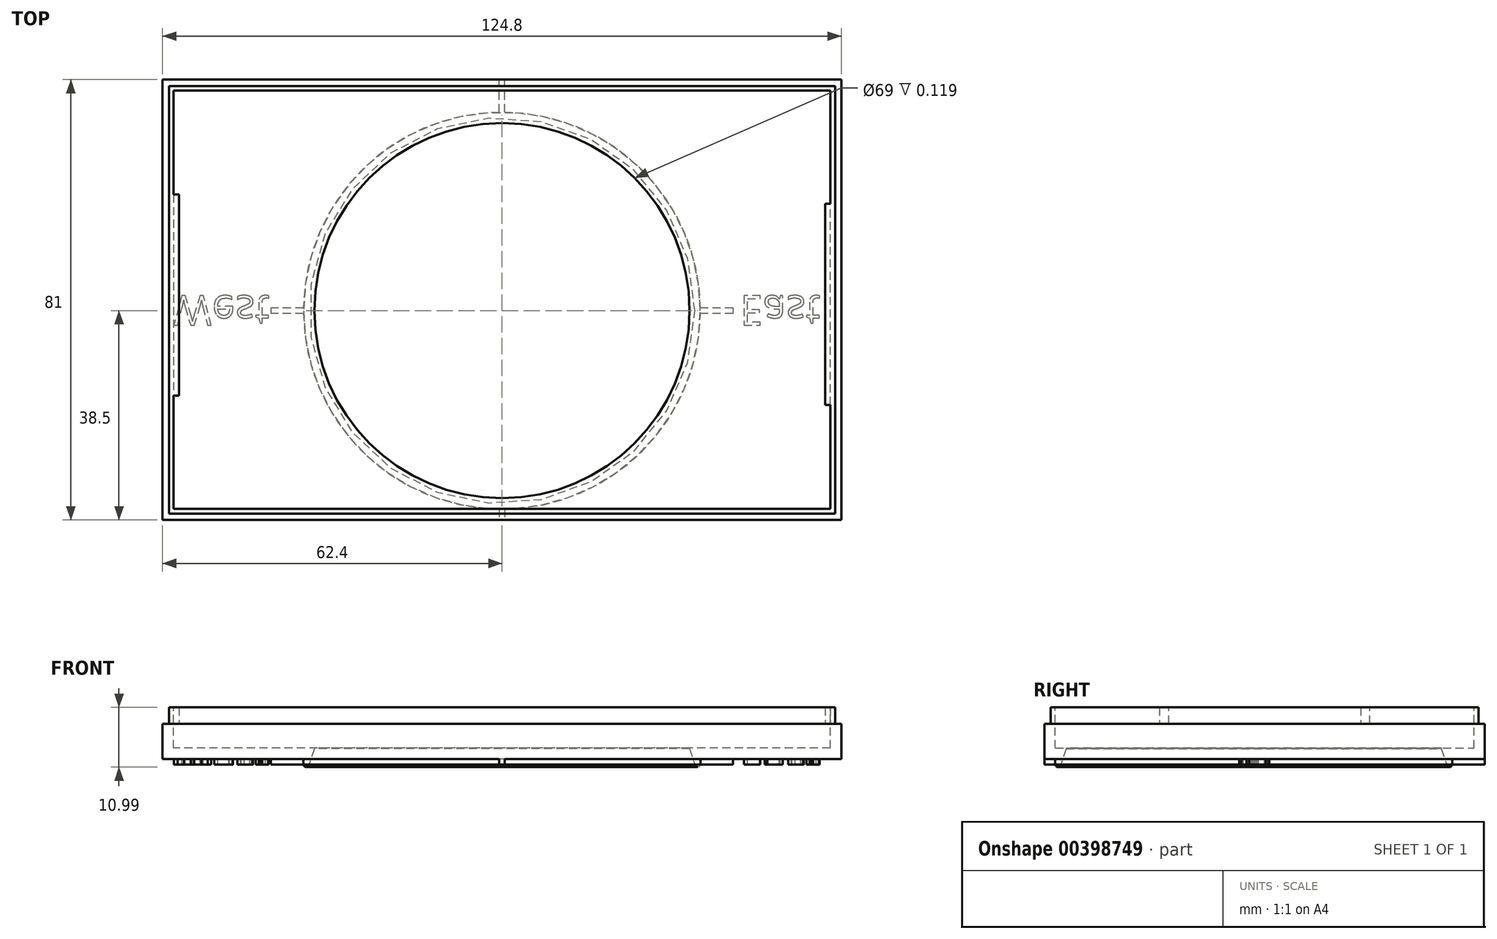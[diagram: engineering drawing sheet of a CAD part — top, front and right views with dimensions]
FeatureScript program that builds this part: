
annotation { "Feature Type Name" : "Feature", "Feature Type Description" : "" }
export const myFeature = defineFeature(function(context is Context, id is Id, definition is map)
    precondition{}
    {
        {
            var Q0;
            Q0=qCreatedBy(makeId("Top.planeOp"),FACE);
            var sketch = newSketch(context, id + "F0", { "sketchPlane" : qUnion([Q0])});
            skLineSegment(sketch, "E0.bottom", {"start": v(62.4, -40.5) * mm, "end": v(-62.4, -40.5) * mm});
            skLineSegment(sketch, "E0.top", {"start": v(62.4, 40.5) * mm, "end": v(-62.4, 40.5) * mm});
            skLineSegment(sketch, "E0.left", {"start": v(62.4, -40.5) * mm, "end": v(62.4, 40.5) * mm});
            skLineSegment(sketch, "E0.right", {"start": v(-62.4, -40.5) * mm, "end": v(-62.4, 40.5) * mm});
            skPoint(sketch, "E0.middle", {"position": v(0, 0) * mm});
            skSolve(sketch);
        }
        {
            var Q0;
            Q0 = qSketchRegion(id + "F0", true);
            extrude(context, id + "F1", {"entities" : qUnion([Q0]), "depth" : 9.5 * mm, "offsetDistance" : 25 * mm});
        }
        {
            var Q0;
            Q0=makeQuery(id+"F1.opExtrude","CAP_FACE",FACE,{"disambiguationData":[OSD([sQuery(id+"F0.wireOp",EDGE,"E0.bottom"),sQuery(id+"F0.wireOp",EDGE,"E0.top"),sQuery(id+"F0.wireOp",EDGE,"E0.left"),sQuery(id+"F0.wireOp",EDGE,"E0.right")])],"isStart":false});
            var sketch = newSketch(context, id + "F2", { "sketchPlane" : qUnion([Q0])});
            skLineSegment(sketch, "E1.bottom", {"start": v(60.4, -38.5) * mm, "end": v(-60.4, -38.5) * mm});
            skLineSegment(sketch, "E1.top", {"start": v(60.4, 38.5) * mm, "end": v(-60.4, 38.5) * mm});
            skLineSegment(sketch, "E1.left", {"start": v(60.4, -38.5) * mm, "end": v(60.4, 38.5) * mm});
            skLineSegment(sketch, "E1.right", {"start": v(-60.4, -38.5) * mm, "end": v(-60.4, 38.5) * mm});
            skPoint(sketch, "E1.middle", {"position": v(0, 0) * mm});
            skSolve(sketch);
        }
        {
            var Q0;
            Q0=makeQuery(id+"F2.imprint","IMPRINT",FACE,{"disambiguationData":[TD([[makeQuery(id+"F2.imprint","IMPRINT",EDGE,{"derivedFrom":sQuery(id+"F2.wireOp",EDGE,"E1.bottom")}),-1.0]])]});
            extrude(context, id + "F3", {"entities" : qUnion([Q0]), "operationType" : NewBodyOperationType.REMOVE, "oppositeDirection" : true, "depth" : 7.5 * mm, "offsetDistance" : 25 * mm});
        }
        {
            var Q0;
            Q0=makeQuery(id+"F1.opExtrude","CAP_FACE",FACE,{"disambiguationData":[OSD([sQuery(id+"F0.wireOp",EDGE,"E0.bottom"),sQuery(id+"F0.wireOp",EDGE,"E0.top"),sQuery(id+"F0.wireOp",EDGE,"E0.left"),sQuery(id+"F0.wireOp",EDGE,"E0.right")])],"isStart":true});
            var sketch = newSketch(context, id + "F4", { "sketchPlane" : qUnion([Q0])});
            skCircle(sketch, "E2", {"center": v(0, 2) * mm, "radius": 36.5 * mm});
            skSolve(sketch);
        }
        {
            var Q0;
            Q0=makeQuery(id+"F4.imprint","IMPRINT",FACE,{"disambiguationData":[TD([[makeQuery(id+"F4.imprint","IMPRINT",EDGE,{"derivedFrom":sQuery(id+"F4.wireOp",EDGE,"E2")}),1.0]])]});
            extrude(context, id + "F5", {"entities" : qUnion([Q0]), "operationType" : NewBodyOperationType.ADD, "depth" : 1 * mm});
        }
        {
            var Q0;
            Q0=makeQuery(id+"F5.opExtrude","CAP_FACE",FACE,{"disambiguationData":[OSD([sQuery(id+"F4.wireOp",EDGE,"E2")])],"isStart":false});
            var sketch = newSketch(context, id + "F6", { "sketchPlane" : qUnion([Q0])});
            skCircle(sketch, "E3", {"center": v(0, 2) * mm, "radius": 34.5 * mm});
            skSolve(sketch);
        }
        {
            var Q0;
            Q0=makeQuery(id+"F6.imprint","IMPRINT",FACE,{"disambiguationData":[TD([[makeQuery(id+"F6.imprint","IMPRINT",EDGE,{"derivedFrom":sQuery(id+"F6.wireOp",EDGE,"E3")}),1.0]])]});
            extrude(context, id + "F7", {"entities" : qUnion([Q0]), "operationType" : NewBodyOperationType.REMOVE, "endBound" : BoundingType.THROUGH_ALL, "oppositeDirection" : true, "depth" : 25 * mm});
        }
        {
            var Q0;
            Q0=qCreatedBy(makeId("Top.planeOp"),FACE);
            var sketch = newSketch(context, id + "F8", { "sketchPlane" : qUnion([Q0])});
            skCircle(sketch, "E4", {"center": v(0, -2) * mm, "radius": 35.5 * mm});
            skSolve(sketch);
        }
        {
            var Q0;
            Q0=qCreatedBy(makeId("Front.planeOp"),FACE);
            var sketch = newSketch(context, id + "F9", { "sketchPlane" : qUnion([Q0])});
            skLineSegment(sketch, "E5", {"start": v(34.42, -1.03) * mm, "end": v(35.42, -1.03) * mm});
            skLineSegment(sketch, "E6", {"start": v(35.42, -1.03) * mm, "end": v(34.39, 2.05) * mm});
            skLineSegment(sketch, "E7", {"start": v(34.39, 2.05) * mm, "end": v(34.42, -1.03) * mm});
            skSolve(sketch);
        }
        {
            var Q0;
            Q0 = qSketchRegion(id + "F9", true);
            var Q1;
            Q1 = qConstructionFilter(qBodyType(qCreatedBy(id + "F8" ,EDGE), BodyType.WIRE), ConstructionObject.NO);
            sweep(context, id + "F10", {"operationType" : NewBodyOperationType.REMOVE, "profiles" : qUnion([Q0]), "path" : qUnion([Q1])});
        }
        {
            var Q0;
            Q0=qCreatedBy(makeId("Top.planeOp"),FACE);
            cPlane(context, id + "F11", {"entities" : qUnion([Q0]), "cplaneType" : CPlaneType.OFFSET, "offset" : 1 * mm, "oppositeDirection" : true, "width" : 150 * mm, "height" : 150 * mm});
        }
        {
            var Q0;
            Q0=qCreatedBy(id+"F11.planeOp",FACE);
            var sketch = newSketch(context, id + "F12", { "sketchPlane" : qUnion([Q0])});
            skCircle(sketch, "E8", {"center": v(0, -2) * mm, "radius": 36 * mm});
            skSolve(sketch);
        }
        {
            var Q0;
            Q0=qCreatedBy(makeId("Front.planeOp"),FACE);
            var sketch = newSketch(context, id + "F13", { "sketchPlane" : qUnion([Q0])});
            skCircle(sketch, "E9", {"center": v(35.91, -1) * mm, "radius": 0.5 * mm});
            skSolve(sketch);
        }
        {
            var Q0;
            Q0=makeQuery(id+"F13.imprint","IMPRINT",FACE,{"disambiguationData":[TD([[makeQuery(id+"F13.imprint","IMPRINT",EDGE,{"derivedFrom":sQuery(id+"F13.wireOp",EDGE,"E9")}),1.0]])]});
            var Q1;
            Q1=sQuery(id+"F12.wireOp",EDGE,"E8");
            revolve(context, id + "F14", {"operationType" : NewBodyOperationType.ADD, "entities" : qUnion([Q0]), "axis" : qUnion([Q1]), "revolveType" : RevolveType.FULL});
        }
        {
            var Q0;
            Q0=makeQuery(id+"F1.opExtrude","CAP_FACE",FACE,{"disambiguationData":[OSD([sQuery(id+"F0.wireOp",EDGE,"E0.bottom"),sQuery(id+"F0.wireOp",EDGE,"E0.top"),sQuery(id+"F0.wireOp",EDGE,"E0.left"),sQuery(id+"F0.wireOp",EDGE,"E0.right")])],"isStart":true});
            var sketch = newSketch(context, id + "F15", { "sketchPlane" : qUnion([Q0])});
            skLineSegment(sketch, "E10.bottom", {"start": v(-36.5, 1.5) * mm, "end": v(-42.5, 1.5) * mm});
            skLineSegment(sketch, "E10.top", {"start": v(-36.5, 2.5) * mm, "end": v(-42.5, 2.5) * mm});
            skLineSegment(sketch, "E10.left", {"start": v(-36.5, 1.5) * mm, "end": v(-36.5, 2.5) * mm});
            skLineSegment(sketch, "E10.right", {"start": v(-42.5, 1.5) * mm, "end": v(-42.5, 2.5) * mm});
            skPoint(sketch, "E10.middle", {"position": v(-39.5, 2) * mm});
            skSolve(sketch);
        }
        {
            var Q0;
            Q0 = qSketchRegion(id + "F15", true);
            extrude(context, id + "F16", {"entities" : qUnion([Q0]), "operationType" : NewBodyOperationType.ADD, "depth" : 1 * mm});
        }
        {
            var Q0;
            Q0=makeQuery(id+"F1.opExtrude","CAP_FACE",FACE,{"disambiguationData":[OSD([sQuery(id+"F0.wireOp",EDGE,"E0.bottom"),sQuery(id+"F0.wireOp",EDGE,"E0.top"),sQuery(id+"F0.wireOp",EDGE,"E0.left"),sQuery(id+"F0.wireOp",EDGE,"E0.right")])],"isStart":true});
            var sketch = newSketch(context, id + "F17", { "sketchPlane" : qUnion([Q0])});
            skLineSegment(sketch, "E11.bottom", {"start": v(42.5, 1.5) * mm, "end": v(36.5, 1.5) * mm});
            skLineSegment(sketch, "E11.top", {"start": v(42.5, 2.5) * mm, "end": v(36.5, 2.5) * mm});
            skLineSegment(sketch, "E11.left", {"start": v(42.5, 1.5) * mm, "end": v(42.5, 2.5) * mm});
            skLineSegment(sketch, "E11.right", {"start": v(36.5, 1.5) * mm, "end": v(36.5, 2.5) * mm});
            skPoint(sketch, "E11.middle", {"position": v(39.5, 2) * mm});
            skSolve(sketch);
        }
        {
            var Q0;
            Q0 = qSketchRegion(id + "F17", true);
            extrude(context, id + "F18", {"entities" : qUnion([Q0]), "operationType" : NewBodyOperationType.ADD, "depth" : 1 * mm});
        }
        {
            var Q0;
            Q0=makeQuery(id+"F1.opExtrude","CAP_FACE",FACE,{"disambiguationData":[OSD([sQuery(id+"F0.wireOp",EDGE,"E0.bottom"),sQuery(id+"F0.wireOp",EDGE,"E0.top"),sQuery(id+"F0.wireOp",EDGE,"E0.left"),sQuery(id+"F0.wireOp",EDGE,"E0.right")])],"isStart":true});
            var sketch = newSketch(context, id + "F19", { "sketchPlane" : qUnion([Q0])});
            skLineSegment(sketch, "E12.bottom", {"start": v(0.5, -34.47) * mm, "end": v(-0.5, -34.47) * mm});
            skLineSegment(sketch, "E12.top", {"start": v(0.5, -40.47) * mm, "end": v(-0.5, -40.47) * mm});
            skLineSegment(sketch, "E12.left", {"start": v(0.5, -34.47) * mm, "end": v(0.5, -40.47) * mm});
            skLineSegment(sketch, "E12.right", {"start": v(-0.5, -34.47) * mm, "end": v(-0.5, -40.47) * mm});
            skPoint(sketch, "E12.middle", {"position": v(0, -37.47) * mm});
            skSolve(sketch);
        }
        {
            var Q0;
            Q0 = qSketchRegion(id + "F19", true);
            extrude(context, id + "F20", {"entities" : qUnion([Q0]), "operationType" : NewBodyOperationType.ADD, "depth" : 1 * mm});
        }
        {
            var Q0;
            Q0=makeQuery(id+"F1.opExtrude","CAP_FACE",FACE,{"disambiguationData":[OSD([sQuery(id+"F0.wireOp",EDGE,"E0.bottom"),sQuery(id+"F0.wireOp",EDGE,"E0.top"),sQuery(id+"F0.wireOp",EDGE,"E0.left"),sQuery(id+"F0.wireOp",EDGE,"E0.right")])],"isStart":true});
            var sketch = newSketch(context, id + "F21", { "sketchPlane" : qUnion([Q0])});
            skLineSegment(sketch, "E13.bottom", {"start": v(0.5, 38.5) * mm, "end": v(-0.5, 38.5) * mm});
            skLineSegment(sketch, "E13.top", {"start": v(0.5, 40.5) * mm, "end": v(-0.5, 40.5) * mm});
            skLineSegment(sketch, "E13.left", {"start": v(0.5, 38.5) * mm, "end": v(0.5, 40.5) * mm});
            skLineSegment(sketch, "E13.right", {"start": v(-0.5, 38.5) * mm, "end": v(-0.5, 40.5) * mm});
            skPoint(sketch, "E13.middle", {"position": v(0, 39.5) * mm});
            skSolve(sketch);
        }
        {
            var Q0;
            Q0 = qSketchRegion(id + "F21", true);
            extrude(context, id + "F22", {"entities" : qUnion([Q0]), "operationType" : NewBodyOperationType.ADD, "depth" : 1 * mm});
        }
        {
            var Q0;
            Q0=makeQuery(id+"F1.opExtrude","CAP_FACE",FACE,{"disambiguationData":[OSD([sQuery(id+"F0.wireOp",EDGE,"E0.bottom"),sQuery(id+"F0.wireOp",EDGE,"E0.top"),sQuery(id+"F0.wireOp",EDGE,"E0.left"),sQuery(id+"F0.wireOp",EDGE,"E0.right")])],"isStart":true});
            var sketch = newSketch(context, id + "F23", { "sketchPlane" : qUnion([Q0])});
            skText(sketch, "E14", { "text": " West", "fontName": "OpenSans-Regular.ttf"});
            const initialGuessF23  = {"E14": [-0.0624, -0.00075, 1, 0, 0.0055]};
            skSetInitialGuess(sketch, initialGuessF23);
            skSolve(sketch);
        }
        {
            var Q0;
            Q0 = qSketchRegion(id + "F23", true);
            extrude(context, id + "F24", {"entities" : qUnion([Q0]), "operationType" : NewBodyOperationType.ADD, "depth" : 1 * mm});
        }
        {
            var Q0;
            {var subQ0=sQuery(id+"F0.wireOp",EDGE,"E0.right");var subQ1=sQuery(id+"F0.wireOp",EDGE,"E0.left");var subQ2=sQuery(id+"F0.wireOp",EDGE,"E0.bottom");var subQ3=sQuery(id+"F0.wireOp",EDGE,"E0.top");Q0=makeQuery(id+"F24.boolean.opBoolean","SPLIT",FACE,{"disambiguationData":[TD([makeQuery(id+"F1.opExtrude","SWEPT_FACE",FACE,{"disambiguationData":[OSD([subQ2])]})])],"derivedFrom":makeQuery(id+"F1.opExtrude","CAP_FACE",FACE,{"disambiguationData":[OSD([subQ2,subQ3,subQ1,subQ0])],"isStart":true})});}
            var sketch = newSketch(context, id + "F25", { "sketchPlane" : qUnion([Q0])});
            skText(sketch, "E15", { "text": "East", "fontName": "OpenSans-Regular.ttf"});
            const initialGuessF25  = {"E15": [0.04373, -0.00075, 1, 0, 0.0055]};
            skSetInitialGuess(sketch, initialGuessF25);
            skSolve(sketch);
        }
        {
            var Q0;
            Q0 = qSketchRegion(id + "F25", true);
            extrude(context, id + "F26", {"entities" : qUnion([Q0]), "operationType" : NewBodyOperationType.ADD, "depth" : 1 * mm});
        }
        {
            var Q0;
            Q0=makeQuery(id+"F1.opExtrude","CAP_FACE",FACE,{"disambiguationData":[OSD([sQuery(id+"F0.wireOp",EDGE,"E0.bottom"),sQuery(id+"F0.wireOp",EDGE,"E0.top"),sQuery(id+"F0.wireOp",EDGE,"E0.left"),sQuery(id+"F0.wireOp",EDGE,"E0.right")])],"isStart":false});
            var sketch = newSketch(context, id + "F27", { "sketchPlane" : qUnion([Q0])});
            skLineSegment(sketch, "E16.bottom", {"start": v(-62.4, -40.5) * mm, "end": v(-61.25, -40.5) * mm});
            skLineSegment(sketch, "E16.top", {"start": v(-62.4, 40.5) * mm, "end": v(-61.25, 40.5) * mm});
            skLineSegment(sketch, "E16.left", {"start": v(-62.4, -40.5) * mm, "end": v(-62.4, 40.5) * mm});
            skLineSegment(sketch, "E16.right", {"start": v(-61.25, -40.5) * mm, "end": v(-61.25, 40.5) * mm});
            skSolve(sketch);
        }
        {
            var Q0;
            Q0 = qSketchRegion(id + "F27", true);
            extrude(context, id + "F28", {"entities" : qUnion([Q0]), "operationType" : NewBodyOperationType.REMOVE, "oppositeDirection" : true, "depth" : 3 * mm, "offsetDistance" : 25 * mm});
        }
        {
            var Q0;
            Q0=makeQuery(id+"F1.opExtrude","CAP_FACE",FACE,{"disambiguationData":[OSD([sQuery(id+"F0.wireOp",EDGE,"E0.bottom"),sQuery(id+"F0.wireOp",EDGE,"E0.top"),sQuery(id+"F0.wireOp",EDGE,"E0.left"),sQuery(id+"F0.wireOp",EDGE,"E0.right")])],"isStart":false});
            var sketch = newSketch(context, id + "F29", { "sketchPlane" : qUnion([Q0])});
            skLineSegment(sketch, "E17.bottom", {"start": v(62.4, -40.5) * mm, "end": v(61.25, -40.5) * mm});
            skLineSegment(sketch, "E17.top", {"start": v(62.4, 40.5) * mm, "end": v(61.25, 40.5) * mm});
            skLineSegment(sketch, "E17.left", {"start": v(62.4, -40.5) * mm, "end": v(62.4, 40.5) * mm});
            skLineSegment(sketch, "E17.right", {"start": v(61.25, -40.5) * mm, "end": v(61.25, 40.5) * mm});
            skSolve(sketch);
        }
        {
            var Q0;
            Q0 = qSketchRegion(id + "F29", true);
            extrude(context, id + "F30", {"entities" : qUnion([Q0]), "operationType" : NewBodyOperationType.REMOVE, "oppositeDirection" : true, "depth" : 3 * mm, "offsetDistance" : 25 * mm});
        }
        {
            var Q0;
            Q0=makeQuery(id+"F1.opExtrude","CAP_FACE",FACE,{"disambiguationData":[OSD([sQuery(id+"F0.wireOp",EDGE,"E0.bottom"),sQuery(id+"F0.wireOp",EDGE,"E0.top"),sQuery(id+"F0.wireOp",EDGE,"E0.left"),sQuery(id+"F0.wireOp",EDGE,"E0.right")])],"isStart":false});
            var sketch = newSketch(context, id + "F31", { "sketchPlane" : qUnion([Q0])});
            skLineSegment(sketch, "E18.bottom", {"start": v(-61.25, 40.5) * mm, "end": v(61.25, 40.5) * mm});
            skLineSegment(sketch, "E18.top", {"start": v(-61.25, 39.35) * mm, "end": v(61.25, 39.35) * mm});
            skLineSegment(sketch, "E18.left", {"start": v(-61.25, 40.5) * mm, "end": v(-61.25, 39.35) * mm});
            skLineSegment(sketch, "E18.right", {"start": v(61.25, 40.5) * mm, "end": v(61.25, 39.35) * mm});
            skSolve(sketch);
        }
        {
            var Q0;
            Q0=makeQuery(id+"F31.imprint","IMPRINT",FACE,{"disambiguationData":[TD([[makeQuery(id+"F31.imprint","IMPRINT",EDGE,{"derivedFrom":sQuery(id+"F31.wireOp",EDGE,"E18.bottom")}),1.0]])]});
            extrude(context, id + "F32", {"entities" : qUnion([Q0]), "operationType" : NewBodyOperationType.REMOVE, "oppositeDirection" : true, "depth" : 3 * mm, "offsetDistance" : 25 * mm});
        }
        {
            var Q0;
            Q0=makeQuery(id+"F1.opExtrude","CAP_FACE",FACE,{"disambiguationData":[OSD([sQuery(id+"F0.wireOp",EDGE,"E0.bottom"),sQuery(id+"F0.wireOp",EDGE,"E0.top"),sQuery(id+"F0.wireOp",EDGE,"E0.left"),sQuery(id+"F0.wireOp",EDGE,"E0.right")])],"isStart":false});
            var sketch = newSketch(context, id + "F33", { "sketchPlane" : qUnion([Q0])});
            skLineSegment(sketch, "E19.bottom", {"start": v(-61.25, -40.5) * mm, "end": v(61.25, -40.5) * mm});
            skLineSegment(sketch, "E19.top", {"start": v(-61.25, -39.35) * mm, "end": v(61.25, -39.35) * mm});
            skLineSegment(sketch, "E19.left", {"start": v(-61.25, -40.5) * mm, "end": v(-61.25, -39.35) * mm});
            skLineSegment(sketch, "E19.right", {"start": v(61.25, -40.5) * mm, "end": v(61.25, -39.35) * mm});
            skSolve(sketch);
        }
        {
            var Q0;
            Q0 = qSketchRegion(id + "F33", true);
            extrude(context, id + "F34", {"entities" : qUnion([Q0]), "operationType" : NewBodyOperationType.REMOVE, "oppositeDirection" : true, "depth" : 3 * mm, "offsetDistance" : 25 * mm});
        }
        {
            var Q0;
            Q0=makeQuery(id+"F30.boolean.opBoolean","COPY",FACE,{"derivedFrom":makeQuery(id+"F30.opExtrude","SWEPT_FACE",FACE,{"disambiguationData":[OSD([sQuery(id+"F29.wireOp",EDGE,"E17.right")])]})});
            var sketch = newSketch(context, id + "F35", { "sketchPlane" : qUnion([Q0])});
            skLineSegment(sketch, "E20.bottom", {"start": v(-19.35, 9.5) * mm, "end": v(17.65, 9.5) * mm});
            skLineSegment(sketch, "E20.top", {"start": v(-19.35, 6.5) * mm, "end": v(17.65, 6.5) * mm});
            skLineSegment(sketch, "E20.left", {"start": v(-19.35, 9.5) * mm, "end": v(-19.35, 6.5) * mm});
            skLineSegment(sketch, "E20.right", {"start": v(17.65, 9.5) * mm, "end": v(17.65, 6.5) * mm});
            skSolve(sketch);
        }
        {
            var Q0;
            Q0 = qSketchRegion(id + "F35", true);
            extrude(context, id + "F36", {"entities" : qUnion([Q0]), "operationType" : NewBodyOperationType.ADD, "oppositeDirection" : true, "depth" : 1.85 * mm, "offsetDistance" : 25 * mm});
        }
        {
            var Q0;
            Q0=makeQuery(id+"F28.boolean.opBoolean","COPY",FACE,{"derivedFrom":makeQuery(id+"F28.opExtrude","SWEPT_FACE",FACE,{"disambiguationData":[OSD([sQuery(id+"F27.wireOp",EDGE,"E16.right")])]})});
            var sketch = newSketch(context, id + "F37", { "sketchPlane" : qUnion([Q0])});
            skLineSegment(sketch, "E21.bottom", {"start": v(-19.35, 9.5) * mm, "end": v(17.65, 9.5) * mm});
            skLineSegment(sketch, "E21.top", {"start": v(-19.35, 6.5) * mm, "end": v(17.65, 6.5) * mm});
            skLineSegment(sketch, "E21.left", {"start": v(-19.35, 9.5) * mm, "end": v(-19.35, 6.5) * mm});
            skLineSegment(sketch, "E21.right", {"start": v(17.65, 9.5) * mm, "end": v(17.65, 6.5) * mm});
            skSolve(sketch);
        }
        {
            var Q0;
            Q0 = qSketchRegion(id + "F37", true);
            extrude(context, id + "F38", {"entities" : qUnion([Q0]), "operationType" : NewBodyOperationType.ADD, "oppositeDirection" : true, "depth" : 1.85 * mm, "offsetDistance" : 25 * mm});
        }
    });
